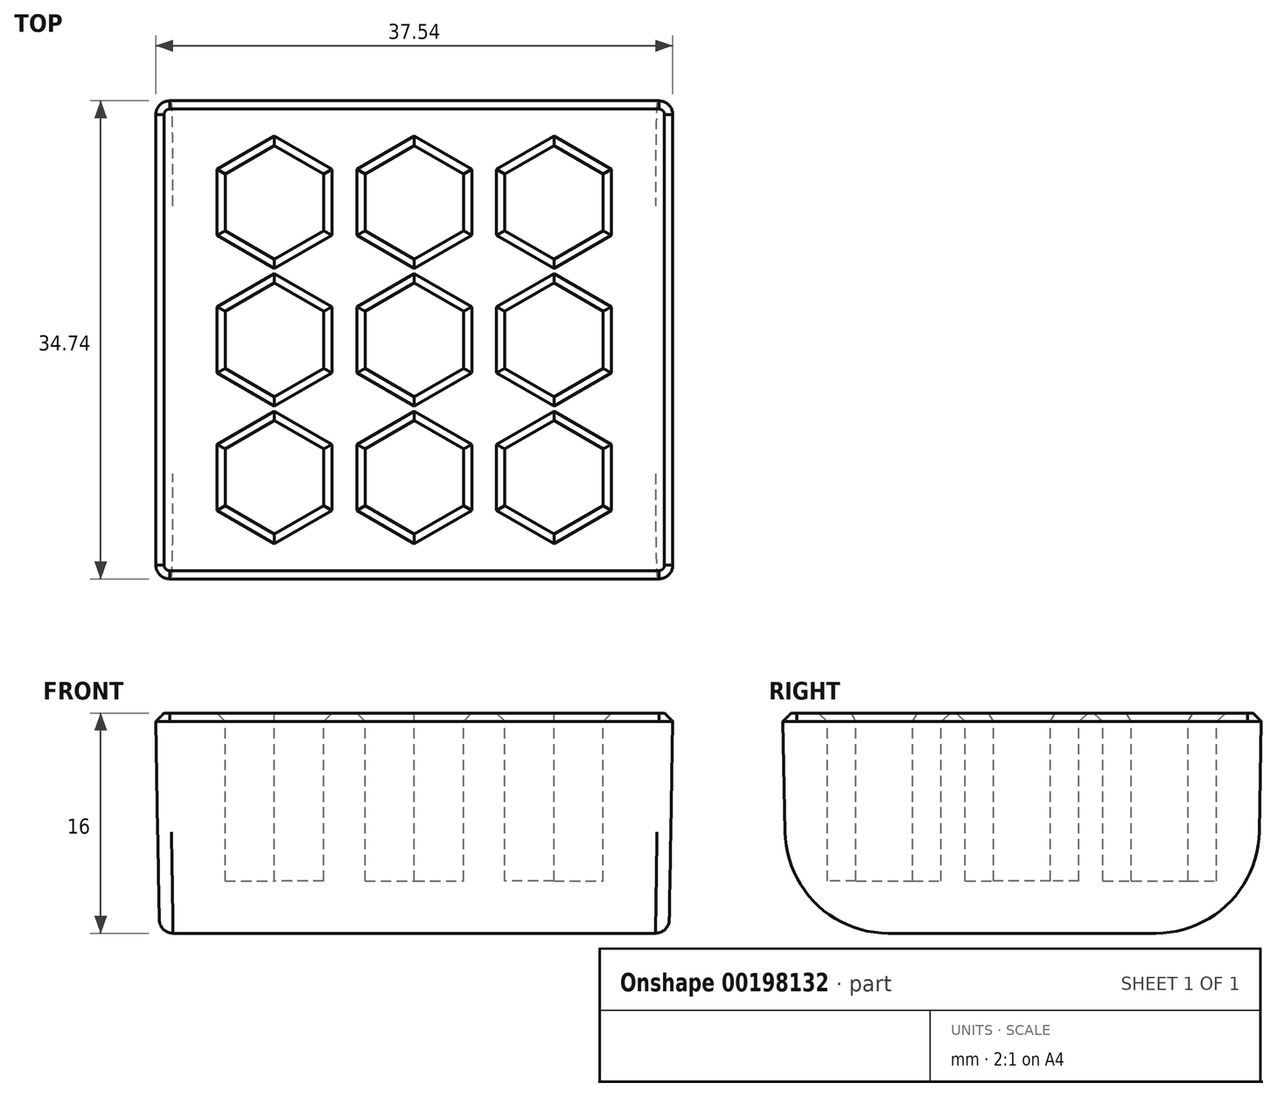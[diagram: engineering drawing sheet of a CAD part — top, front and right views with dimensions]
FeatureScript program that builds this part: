
annotation { "Feature Type Name" : "Feature", "Feature Type Description" : "" }
export const myFeature = defineFeature(function(context is Context, id is Id, definition is map)
    precondition{}
    {
        {
            var Q0;
            Q0=qCreatedBy(makeId("Top.planeOp"),FACE);
            var sketch = newSketch(context, id + "F0", { "sketchPlane" : qUnion([Q0])});
            skLineSegment(sketch, "E0.bottom", {"start": v(18.5, 17.1) * mm, "end": v(-18.5, 17.1) * mm});
            skLineSegment(sketch, "E0.top", {"start": v(18.5, -17.1) * mm, "end": v(-18.5, -17.1) * mm});
            skLineSegment(sketch, "E0.left", {"start": v(18.5, 17.1) * mm, "end": v(18.5, -17.1) * mm});
            skLineSegment(sketch, "E0.right", {"start": v(-18.5, 17.1) * mm, "end": v(-18.5, -17.1) * mm});
            skPoint(sketch, "E0.middle", {"position": v(0, 0) * mm});
            skSolve(sketch);
        }
        {
            var Q0;
            Q0=makeQuery(id+"F0.imprint","IMPRINT",FACE,{"disambiguationData":[TD([[makeQuery(id+"F0.imprint","IMPRINT",EDGE,{"derivedFrom":sQuery(id+"F0.wireOp",EDGE,"E0.bottom")}),1.0]])]});
            extrude(context, id + "F1", {"entities" : qUnion([Q0]), "depth" : (25 - 13 + 4) * mm, "hasDraft" : true, "draftAngle" : 1 * degree});
        }
        {
            var Q0;
            Q0=makeQuery(id+"F1.opExtrude","CAP_EDGE",EDGE,{"disambiguationData":[OSD([sQuery(id+"F0.wireOp",EDGE,"E0.top")])],"isStart":true});
            var Q1;
            Q1=makeQuery(id+"F1.opExtrude","CAP_EDGE",EDGE,{"disambiguationData":[OSD([sQuery(id+"F0.wireOp",EDGE,"E0.bottom")])],"isStart":true});
            fillet(context, id + "F2", {"entities" : qUnion([Q0, Q1]), "radius" : 7.5 * mm, "tangentPropagation" : true, "allowEdgeOverflow" : false});
        }
        {
            var Q0;
            Q0=makeQuery(id+"F1.opExtrude","SWEPT_EDGE",EDGE,{"disambiguationData":[OSD([sQuery(id+"F0.wireOp",EDGE,"E0.top"),sQuery(id+"F0.wireOp",EDGE,"E0.left")])]});
            var Q1;
            Q1=makeQuery(id+"F1.opExtrude","SWEPT_EDGE",EDGE,{"disambiguationData":[OSD([sQuery(id+"F0.wireOp",EDGE,"E0.top"),sQuery(id+"F0.wireOp",EDGE,"E0.right")])]});
            fillet(context, id + "F3", {"entities" : qUnion([Q0, Q1]), "radius" : 1 * mm, "tangentPropagation" : true, "allowEdgeOverflow" : false});
        }
        {
            var Q0;
            Q0=makeQuery(id+"F1.opExtrude","CAP_FACE",FACE,{"disambiguationData":[OSD([sQuery(id+"F0.wireOp",EDGE,"E0.bottom"),sQuery(id+"F0.wireOp",EDGE,"E0.top"),sQuery(id+"F0.wireOp",EDGE,"E0.left"),sQuery(id+"F0.wireOp",EDGE,"E0.right")])],"isStart":false});
            var sketch = newSketch(context, id + "F4", { "sketchPlane" : qUnion([Q0])});
            skLineSegment(sketch, "E1", {"start": v(0, 17.38) * mm, "end": v(0, -17.38) * mm, "construction": true});
            skLineSegment(sketch, "E2", {"start": v(-18.78, 0) * mm, "end": v(18.78, 0) * mm, "construction": true});
            skCircle(sketch, "E3.cCircle", {"center": v(0, 0) * mm, "radius": 3.57 * mm, "construction": true});
            skLineSegment(sketch, "E3.0", {"start": v(3.58, 2.06) * mm, "end": v(3.58, -2.06) * mm});
            skLineSegment(sketch, "E3.1", {"start": v(3.58, -2.06) * mm, "end": v(0, -4.13) * mm});
            skLineSegment(sketch, "E3.2", {"start": v(0, -4.13) * mm, "end": v(-3.57, -2.06) * mm});
            skLineSegment(sketch, "E3.3", {"start": v(-3.57, -2.06) * mm, "end": v(-3.57, 2.06) * mm});
            skLineSegment(sketch, "E3.4", {"start": v(-3.57, 2.06) * mm, "end": v(0, 4.13) * mm});
            skLineSegment(sketch, "E3.5", {"start": v(0, 4.13) * mm, "end": v(3.58, 2.06) * mm});
            skPoint(sketch, "E3.0.midPoint", {"position": v(3.58, 0) * mm});
            skLineSegment(sketch, "E4.0.1.0", {"start": v(-3.57, 12.06) * mm, "end": v(0, 14.13) * mm});
            skLineSegment(sketch, "E4.0.1.1", {"start": v(-3.57, 7.94) * mm, "end": v(-3.57, 12.06) * mm});
            skLineSegment(sketch, "E4.0.1.2", {"start": v(0, 5.87) * mm, "end": v(-3.57, 7.94) * mm});
            skCircle(sketch, "E4.0.1.3", {"center": v(0, 10) * mm, "radius": 3.57 * mm, "construction": true});
            skLineSegment(sketch, "E4.0.1.4", {"start": v(3.58, 7.94) * mm, "end": v(0, 5.87) * mm});
            skLineSegment(sketch, "E4.0.1.5", {"start": v(3.58, 12.06) * mm, "end": v(3.58, 7.94) * mm});
            skLineSegment(sketch, "E4.0.1.6", {"start": v(0, 14.13) * mm, "end": v(3.58, 12.06) * mm});
            skLineSegment(sketch, "E4.1.0.0", {"start": v(6.57, 2.06) * mm, "end": v(10.15, 4.13) * mm});
            skLineSegment(sketch, "E4.1.0.1", {"start": v(6.58, -2.06) * mm, "end": v(6.58, 2.06) * mm});
            skLineSegment(sketch, "E4.1.0.2", {"start": v(10.15, -4.13) * mm, "end": v(6.58, -2.06) * mm});
            skCircle(sketch, "E4.1.0.3", {"center": v(10.15, 0) * mm, "radius": 3.57 * mm, "construction": true});
            skLineSegment(sketch, "E4.1.0.4", {"start": v(13.73, -2.06) * mm, "end": v(10.15, -4.13) * mm});
            skLineSegment(sketch, "E4.1.0.5", {"start": v(13.73, 2.06) * mm, "end": v(13.73, -2.06) * mm});
            skLineSegment(sketch, "E4.1.0.6", {"start": v(10.15, 4.13) * mm, "end": v(13.73, 2.06) * mm});
            skLineSegment(sketch, "E4.1.1.0", {"start": v(6.57, 12.06) * mm, "end": v(10.15, 14.13) * mm});
            skLineSegment(sketch, "E4.1.1.1", {"start": v(6.58, 7.94) * mm, "end": v(6.58, 12.06) * mm});
            skLineSegment(sketch, "E4.1.1.2", {"start": v(10.15, 5.87) * mm, "end": v(6.58, 7.94) * mm});
            skCircle(sketch, "E4.1.1.3", {"center": v(10.15, 10) * mm, "radius": 3.57 * mm, "construction": true});
            skLineSegment(sketch, "E4.1.1.4", {"start": v(13.73, 7.94) * mm, "end": v(10.15, 5.87) * mm});
            skLineSegment(sketch, "E4.1.1.5", {"start": v(13.73, 12.06) * mm, "end": v(13.73, 7.94) * mm});
            skLineSegment(sketch, "E4.1.1.6", {"start": v(10.15, 14.13) * mm, "end": v(13.73, 12.06) * mm});
            skLineSegment(sketch, "E4.direction1", {"start": v(-3.57, 2.06) * mm, "end": v(6.58, 2.06) * mm, "construction": true});
            skLineSegment(sketch, "E4.direction2", {"start": v(-3.57, 2.06) * mm, "end": v(-3.57, 12.06) * mm, "construction": true});
            skLineSegment(sketch, "E5.MirrorCS", {"start": v(-6.57, 7.94) * mm, "end": v(-6.57, 12.06) * mm});
            skLineSegment(sketch, "E6.MirrorCS", {"start": v(-6.57, 12.06) * mm, "end": v(-10.15, 14.13) * mm});
            skCircle(sketch, "E7.MirrorC", {"center": v(-10.15, 10) * mm, "radius": 3.57 * mm, "construction": true});
            skLineSegment(sketch, "E8.MirrorCS", {"start": v(-10.15, 14.13) * mm, "end": v(-13.72, 12.06) * mm});
            skLineSegment(sketch, "E9.MirrorCS", {"start": v(-13.72, 12.06) * mm, "end": v(-13.72, 7.94) * mm});
            skLineSegment(sketch, "E10.MirrorCS", {"start": v(-13.72, 7.94) * mm, "end": v(-10.15, 5.87) * mm});
            skLineSegment(sketch, "E11.MirrorCS", {"start": v(-10.15, 5.87) * mm, "end": v(-6.58, 7.94) * mm});
            skLineSegment(sketch, "E12.MirrorCS", {"start": v(-6.57, 2.06) * mm, "end": v(-10.15, 4.13) * mm});
            skLineSegment(sketch, "E13.MirrorCS", {"start": v(-10.15, 4.13) * mm, "end": v(-13.72, 2.06) * mm});
            skCircle(sketch, "E14.MirrorC", {"center": v(-10.15, 0) * mm, "radius": 3.57 * mm, "construction": true});
            skLineSegment(sketch, "E15.MirrorCS", {"start": v(-13.72, 2.06) * mm, "end": v(-13.72, -2.06) * mm});
            skLineSegment(sketch, "E16.MirrorCS", {"start": v(-13.72, -2.06) * mm, "end": v(-10.15, -4.13) * mm});
            skLineSegment(sketch, "E17.MirrorCS", {"start": v(-10.15, -4.13) * mm, "end": v(-6.58, -2.06) * mm});
            skLineSegment(sketch, "E18.MirrorCS", {"start": v(-6.57, -2.06) * mm, "end": v(-6.57, 2.06) * mm});
            skCircle(sketch, "E19.MirrorC", {"center": v(-10.15, -10) * mm, "radius": 3.57 * mm, "construction": true});
            skLineSegment(sketch, "E20.MirrorCS", {"start": v(-13.72, -7.94) * mm, "end": v(-10.15, -5.87) * mm});
            skLineSegment(sketch, "E21.MirrorCS", {"start": v(-10.15, -5.87) * mm, "end": v(-6.57, -7.94) * mm});
            skLineSegment(sketch, "E22.MirrorCS", {"start": v(-6.57, -7.94) * mm, "end": v(-6.57, -12.06) * mm});
            skLineSegment(sketch, "E23.MirrorCS", {"start": v(-6.58, -12.06) * mm, "end": v(-10.15, -14.13) * mm});
            skLineSegment(sketch, "E24.MirrorCS", {"start": v(-10.15, -14.13) * mm, "end": v(-13.72, -12.06) * mm});
            skLineSegment(sketch, "E25.MirrorCS", {"start": v(-13.72, -12.06) * mm, "end": v(-13.72, -7.94) * mm});
            skLineSegment(sketch, "E26.MirrorCS", {"start": v(6.58, -7.94) * mm, "end": v(6.58, -12.06) * mm});
            skLineSegment(sketch, "E27.MirrorCS", {"start": v(6.58, -12.06) * mm, "end": v(10.15, -14.13) * mm});
            skLineSegment(sketch, "E28.MirrorCS", {"start": v(10.15, -14.13) * mm, "end": v(13.73, -12.06) * mm});
            skCircle(sketch, "E29.MirrorC", {"center": v(10.15, -10) * mm, "radius": 3.57 * mm, "construction": true});
            skLineSegment(sketch, "E30.MirrorCS", {"start": v(13.73, -12.06) * mm, "end": v(13.73, -7.94) * mm});
            skLineSegment(sketch, "E31.MirrorCS", {"start": v(13.73, -7.94) * mm, "end": v(10.15, -5.87) * mm});
            skLineSegment(sketch, "E32.MirrorCS", {"start": v(10.15, -5.87) * mm, "end": v(6.57, -7.94) * mm});
            skCircle(sketch, "E33.MirrorC", {"center": v(0, -10) * mm, "radius": 3.57 * mm, "construction": true});
            skLineSegment(sketch, "E34.MirrorCS", {"start": v(3.58, -7.94) * mm, "end": v(0, -5.87) * mm});
            skLineSegment(sketch, "E35.MirrorCS", {"start": v(0, -5.87) * mm, "end": v(-3.57, -7.94) * mm});
            skLineSegment(sketch, "E36.MirrorCS", {"start": v(-3.57, -2.06) * mm, "end": v(-3.57, -12.06) * mm, "construction": true});
            skLineSegment(sketch, "E37.MirrorCS", {"start": v(-3.57, -12.06) * mm, "end": v(0, -14.13) * mm});
            skLineSegment(sketch, "E38.MirrorCS", {"start": v(0, -14.13) * mm, "end": v(3.58, -12.06) * mm});
            skLineSegment(sketch, "E39.MirrorCS", {"start": v(3.58, -12.06) * mm, "end": v(3.58, -7.94) * mm});
            skLineSegment(sketch, "E40", {"start": v(-3.57, -7.94) * mm, "end": v(-3.57, -12.06) * mm});
            skSolve(sketch);
        }
        {
            var Q0;
            Q0=qSketchRegion(id+"F4",true);
            extrude(context, id + "F5", {"entities" : qUnion([Q0]), "operationType" : NewBodyOperationType.REMOVE, "oppositeDirection" : true, "depth" : 12.2 * mm});
        }
        {
            var Q0;
            Q0=makeQuery(id+"F1.opExtrude","CAP_FACE",FACE,{"disambiguationData":[OSD([sQuery(id+"F0.wireOp",EDGE,"E0.bottom"),sQuery(id+"F0.wireOp",EDGE,"E0.top"),sQuery(id+"F0.wireOp",EDGE,"E0.left"),sQuery(id+"F0.wireOp",EDGE,"E0.right")])],"isStart":false});
            chamfer(context, id + "F6", {"entities" : qUnion([Q0]), "width" : .6 * mm, "tangentPropagation" : true});
        }
    });
